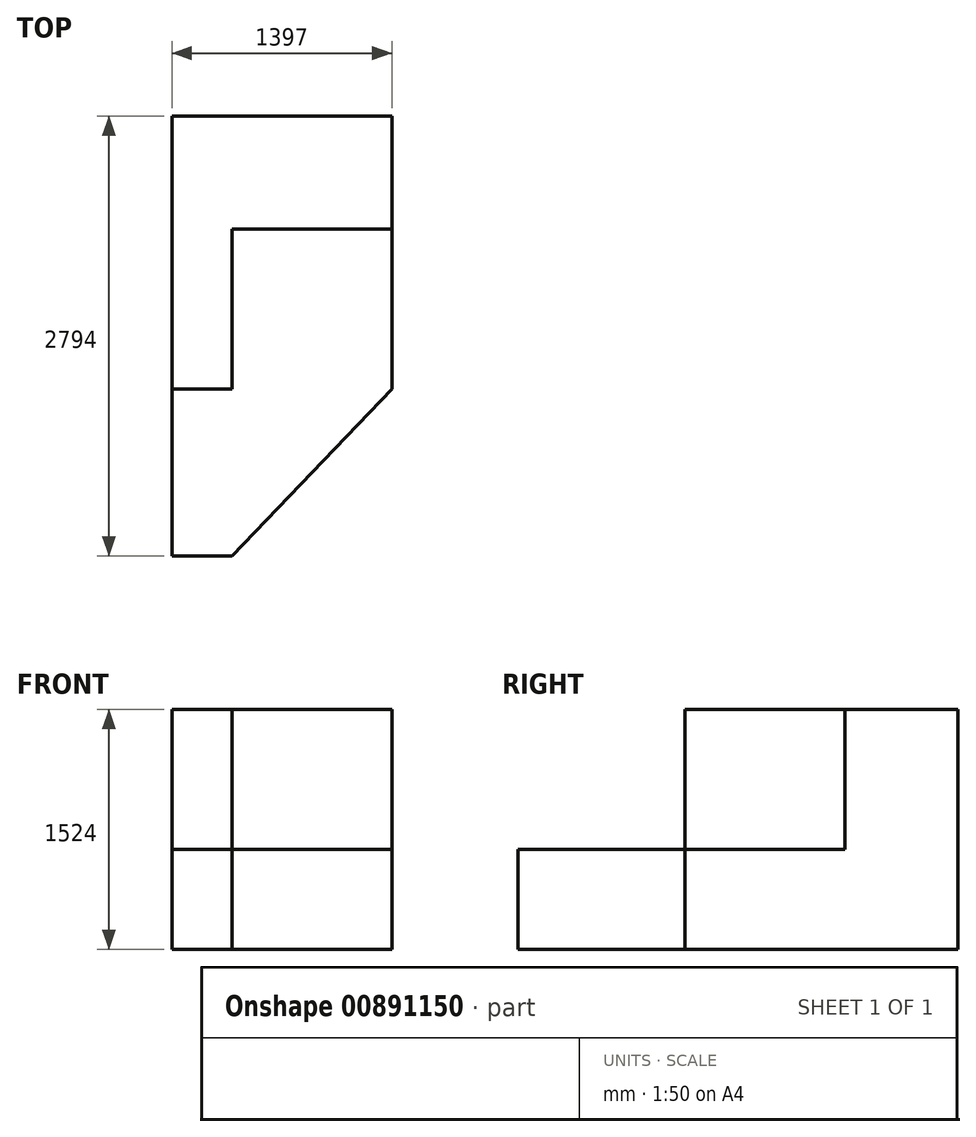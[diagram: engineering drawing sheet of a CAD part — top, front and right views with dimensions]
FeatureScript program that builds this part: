
annotation { "Feature Type Name" : "Feature", "Feature Type Description" : "" }
export const myFeature = defineFeature(function(context is Context, id is Id, definition is map)
    precondition{}
    {
        {
            var Q0;
            Q0=qCreatedBy(makeId("Top.planeOp"),FACE);
            var sketch = newSketch(context, id + "F0", { "sketchPlane" : qUnion([Q0])});
            skLineSegment(sketch, "E0.bottom", {"start": v(0, 0) * mm, "end": v(-1397, 0) * mm});
            skLineSegment(sketch, "E0.top", {"start": v(0, -2794) * mm, "end": v(-1397, -2794) * mm});
            skLineSegment(sketch, "E0.left", {"start": v(0, 0) * mm, "end": v(0, -2794) * mm});
            skLineSegment(sketch, "E0.right", {"start": v(-1397, 0) * mm, "end": v(-1397, -2794) * mm});
            skSolve(sketch);
        }
        {
            var Q0;
            Q0=qSketchRegion(id+"F0",true);
            extrude(context, id + "F1", {"entities" : qUnion([Q0]), "depth" : 635 * mm, "offsetDistance" : 25.4 * mm});
        }
        {
            var Q0;
            Q0=makeQuery(id+"F1.opExtrude","CAP_FACE",FACE,{"disambiguationData":[OSD([sQuery(id+"F0.wireOp",EDGE,"E0.bottom"),sQuery(id+"F0.wireOp",EDGE,"E0.top"),sQuery(id+"F0.wireOp",EDGE,"E0.left"),sQuery(id+"F0.wireOp",EDGE,"E0.right")])],"isStart":false});
            var sketch = newSketch(context, id + "F2", { "sketchPlane" : qUnion([Q0])});
            skLineSegment(sketch, "E1.bottom", {"start": v(-1397, 0) * mm, "end": v(0, 0) * mm});
            skLineSegment(sketch, "E1.top", {"start": v(-1397, -716.89) * mm, "end": v(0, -716.89) * mm});
            skLineSegment(sketch, "E1.left", {"start": v(-1397, 0) * mm, "end": v(-1397, -716.89) * mm});
            skLineSegment(sketch, "E1.right", {"start": v(0, 0) * mm, "end": v(0, -716.89) * mm});
            skSolve(sketch);
        }
        {
            var Q0;
            Q0=qSketchRegion(id+"F2",true);
            extrude(context, id + "F3", {"entities" : qUnion([Q0]), "operationType" : NewBodyOperationType.ADD, "depth" : 889 * mm, "offsetDistance" : 25.4 * mm});
        }
        {
            var Q0;
            Q0=makeQuery(id+"F1.opExtrude","CAP_FACE",FACE,{"disambiguationData":[OSD([sQuery(id+"F0.wireOp",EDGE,"E0.bottom"),sQuery(id+"F0.wireOp",EDGE,"E0.top"),sQuery(id+"F0.wireOp",EDGE,"E0.left"),sQuery(id+"F0.wireOp",EDGE,"E0.right")])],"isStart":false});
            var sketch = newSketch(context, id + "F4", { "sketchPlane" : qUnion([Q0])});
            skLineSegment(sketch, "E2.bottom", {"start": v(-1397, -716.89) * mm, "end": v(-1016, -716.89) * mm});
            skLineSegment(sketch, "E2.top", {"start": v(-1397, -1732.89) * mm, "end": v(-1016, -1732.89) * mm});
            skLineSegment(sketch, "E2.left", {"start": v(-1397, -716.89) * mm, "end": v(-1397, -1732.89) * mm});
            skLineSegment(sketch, "E2.right", {"start": v(-1016, -716.89) * mm, "end": v(-1016, -1732.89) * mm});
            skSolve(sketch);
        }
        {
            var Q0;
            Q0=qSketchRegion(id+"F4",true);
            extrude(context, id + "F5", {"entities" : qUnion([Q0]), "operationType" : NewBodyOperationType.ADD, "depth" : 889 * mm, "offsetDistance" : 25.4 * mm});
        }
        {
            var Q0;
            Q0=makeQuery(id+"F1.opExtrude","CAP_FACE",FACE,{"disambiguationData":[OSD([sQuery(id+"F0.wireOp",EDGE,"E0.bottom"),sQuery(id+"F0.wireOp",EDGE,"E0.top"),sQuery(id+"F0.wireOp",EDGE,"E0.left"),sQuery(id+"F0.wireOp",EDGE,"E0.right")])],"isStart":false});
            var sketch = newSketch(context, id + "F6", { "sketchPlane" : qUnion([Q0])});
            skLineSegment(sketch, "E3", {"start": v(-1016, -1732.89) * mm, "end": v(0, -1732.89) * mm});
            skLineSegment(sketch, "E4", {"start": v(-1016, -1732.89) * mm, "end": v(-1016, -2794) * mm});
            skLineSegment(sketch, "E5", {"start": v(-1016, -2794) * mm, "end": v(0, -1732.89) * mm});
            skSolve(sketch);
        }
        {
            var Q0;
            {var subQ0=sQuery(id+"F6.wireOp",EDGE,"E5");Q0=makeQuery(id+"F6.imprint","IMPRINT",FACE,{"disambiguationData":[TD([[makeQuery(id+"F6.imprint","IMPRINT",EDGE,{"derivedFrom":subQ0}),-1.0]])]});}
            extrude(context, id + "F7", {"entities" : qUnion([Q0]), "operationType" : NewBodyOperationType.REMOVE, "oppositeDirection" : true, "depth" : 635 * mm, "offsetDistance" : 25.4 * mm});
        }
    });
